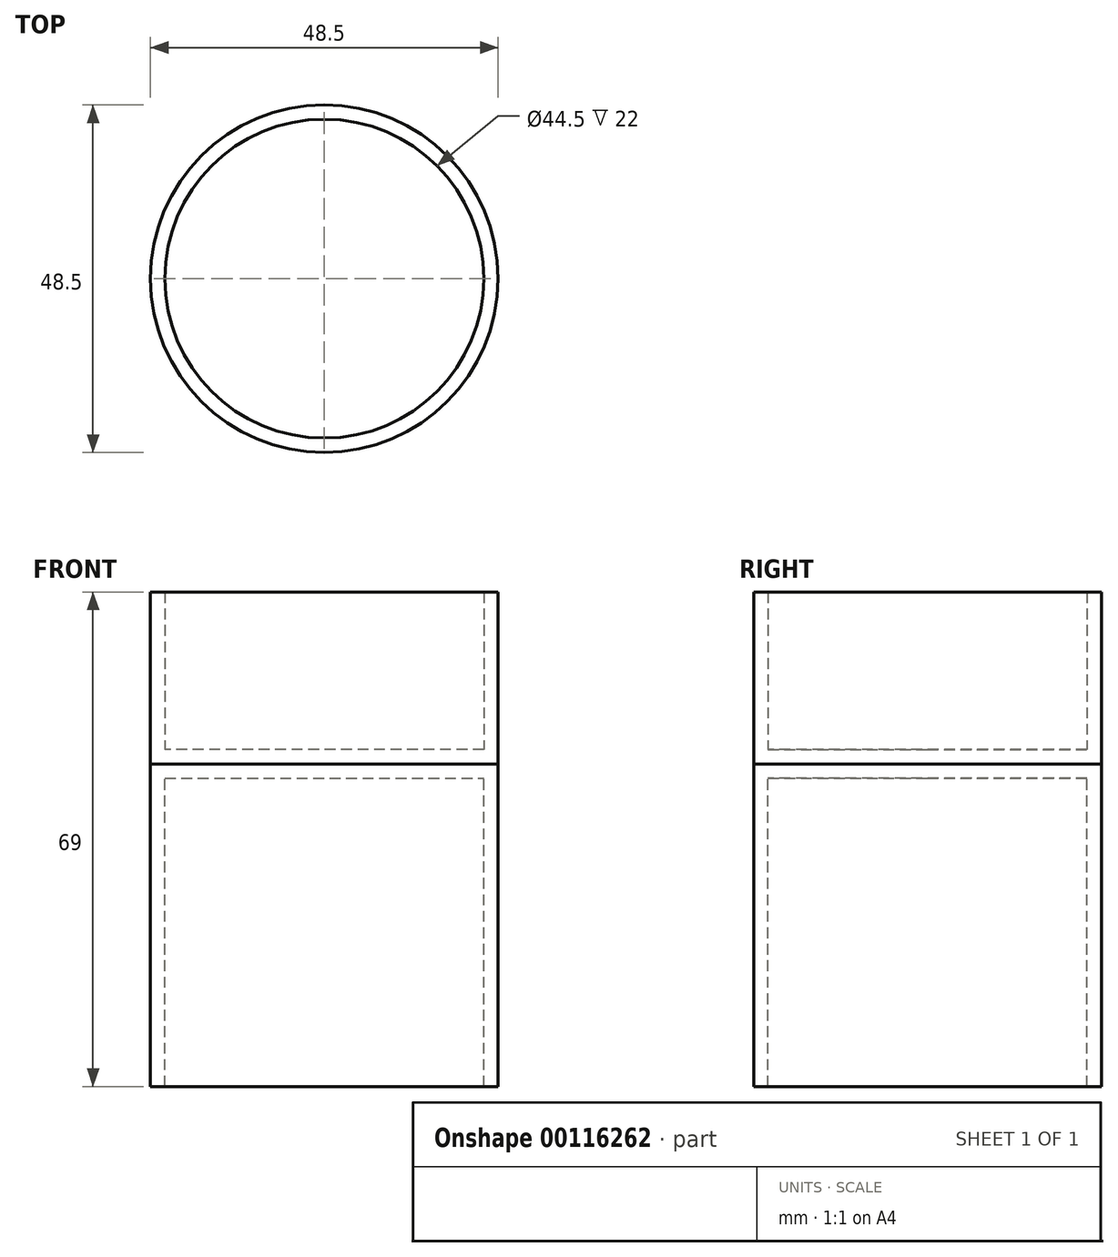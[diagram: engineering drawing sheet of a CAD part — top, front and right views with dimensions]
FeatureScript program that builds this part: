
annotation { "Feature Type Name" : "Feature", "Feature Type Description" : "" }
export const myFeature = defineFeature(function(context is Context, id is Id, definition is map)
    precondition{}
    {
        {
            var Q0;
            Q0=qCreatedBy(makeId("Top.planeOp"),FACE);
            var sketch = newSketch(context, id + "F0", { "sketchPlane" : qUnion([Q0])});
            skCircle(sketch, "E0", {"center": v(0, 0) * mm, "radius": 24.25 * mm});
            skSolve(sketch);
        }
        {
            var Q0;
            Q0=qSketchRegion(id+"F0",true);
            extrude(context, id + "F1", {"entities" : qUnion([Q0]), "depth" : 24 * mm});
        }
        {
            var Q0;
            Q0=makeQuery(id+"F1.opExtrude","CAP_FACE",FACE,{"disambiguationData":[OSD([sQuery(id+"F0.wireOp",EDGE,"E0")])],"isStart":false});
            shell(context, id + "F2", {"entities" : qUnion([Q0]), "thickness" : 2 * mm});
        }
        {
            var Q0;
            Q0=makeQuery(id+"F1.opExtrude","CAP_FACE",FACE,{"disambiguationData":[OSD([sQuery(id+"F0.wireOp",EDGE,"E0")])],"isStart":true});
            var sketch = newSketch(context, id + "F3", { "sketchPlane" : qUnion([Q0])});
            skCircle(sketch, "E1", {"center": v(0, 0) * mm, "radius": 24.25 * mm});
            skSolve(sketch);
        }
        {
            var Q0;
            Q0=qSketchRegion(id+"F3",true);
            extrude(context, id + "F4", {"entities" : qUnion([Q0]), "depth" : 45 * mm});
        }
        {
            var Q0;
            Q0=makeQuery(id+"F4.opExtrude","CAP_FACE",FACE,{"disambiguationData":[OSD([sQuery(id+"F3.wireOp",EDGE,"E1")])],"isStart":false});
            shell(context, id + "F5", {"entities" : qUnion([Q0]), "thickness" : 2 * mm});
        }
    });
